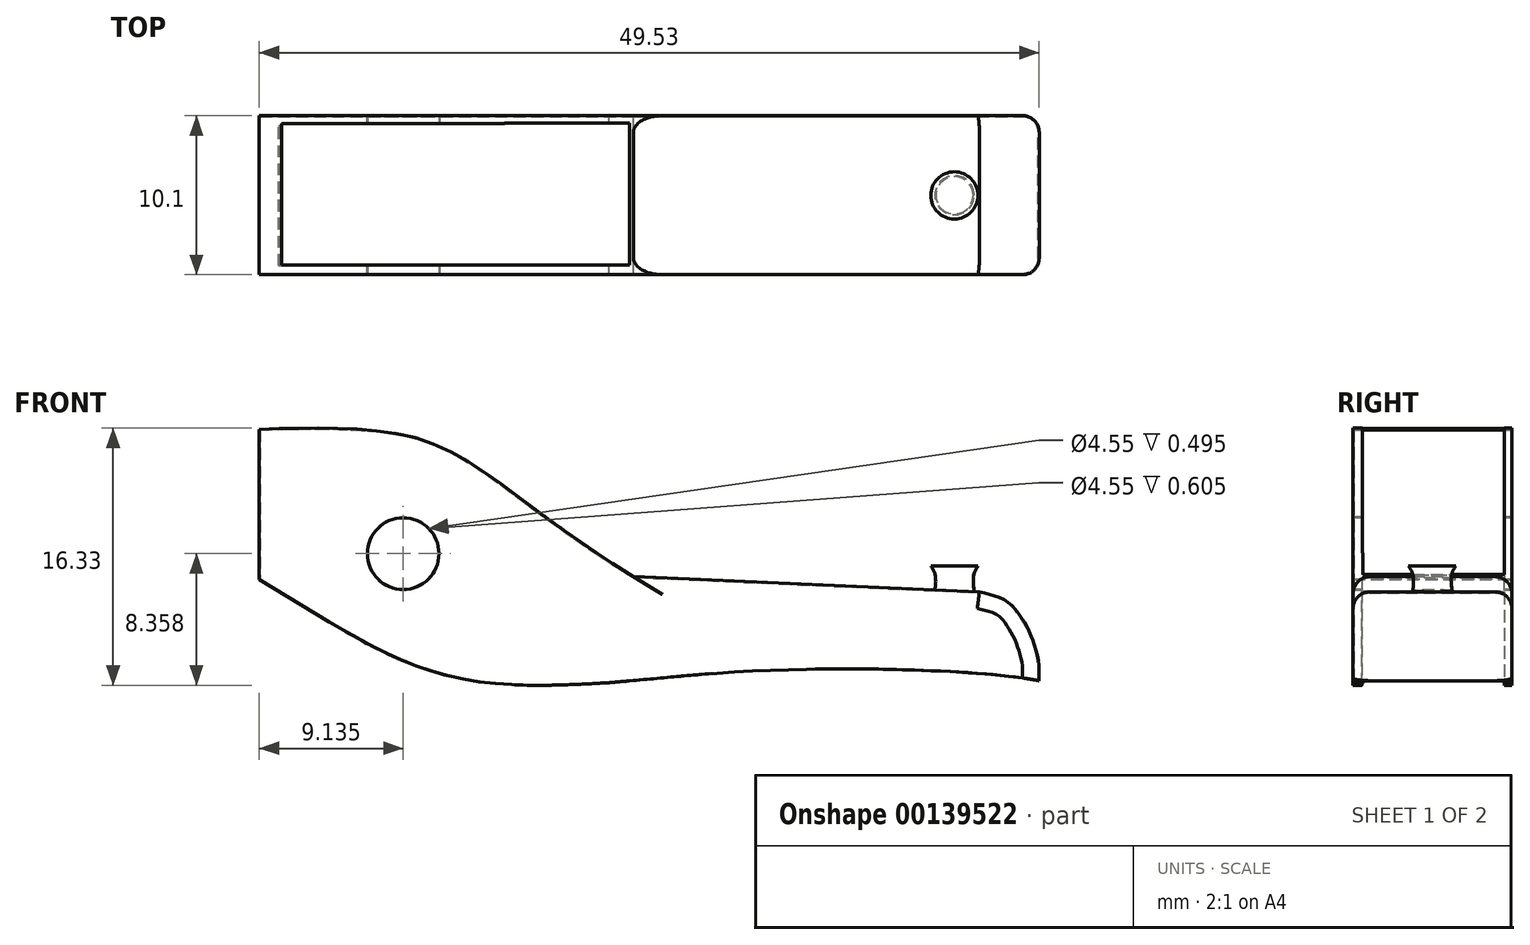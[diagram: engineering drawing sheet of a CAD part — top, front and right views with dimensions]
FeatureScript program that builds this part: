
annotation { "Feature Type Name" : "Feature", "Feature Type Description" : "" }
export const myFeature = defineFeature(function(context is Context, id is Id, definition is map)
    precondition{}
    {
        {
            var Q0;
            Q0=qCreatedBy(makeId("Front.planeOp"),FACE);
            var sketch = newSketch(context, id + "F0", { "sketchPlane" : qUnion([Q0])});
            skLineSegment(sketch, "E0", {"start": v(-18.11, 14.62) * mm, "end": v(-18.11, 5.15) * mm});
            skFitSpline(sketch, "E1", {"points": [v(-18.11, 14.62) * mm, v(-5.7, 13.04) * mm, v(5.6, 5.26) * mm], "startDerivative": vector(43.3, 1.46) * mm, "endDerivative": vector(32.79, -20.12) * mm});
            skFitSpline(sketch, "E2", {"points": [v(-18.11, 5.15) * mm, v(-6.1, -0.96) * mm, v(5.6, -1.29) * mm], "startDerivative": vector(24.76, -14.65) * mm, "endDerivative": vector(22.2, 1.12) * mm});
            skLineSegment(sketch, "E3", {"start": v(-5.7, 13.04) * mm, "end": v(-6.1, -0.96) * mm, "construction": true});
            skFitSpline(sketch, "E4", {"points": [v(5.6, -1.29) * mm, v(15.63, -0.6) * mm, v(31.3, -1.29) * mm], "startDerivative": vector(20.89, 1.84) * mm, "endDerivative": vector(17.9, -3.47) * mm});
            skLineSegment(sketch, "E5", {"start": v(5.6, 5.26) * mm, "end": v(27.57, 4.28) * mm});
            skFitSpline(sketch, "E6", {"points": [v(27.57, 4.28) * mm, v(29.94, 3.06) * mm, v(31.3, -1.29) * mm], "startDerivative": vector(9.56, -2.1) * mm, "endDerivative": vector(-1.08, -8.77) * mm});
            skLineSegment(sketch, "E7", {"start": v(-18.11, 14.62) * mm, "end": v(31.89, 14.62) * mm, "construction": true});
            skLineSegment(sketch, "E8", {"start": v(31.89, 14.62) * mm, "end": v(31.3, -1.29) * mm, "construction": true});
            skSolve(sketch);
        }
        {
            var Q0;
            Q0 = qSketchRegion(id + "F0", true);
            extrude(context, id + "F1", {"entities" : qUnion([Q0]), "depth" : 10 * mm});
        }
        {
            var Q0;
            Q0=makeQuery(id+"F1.opExtrude","CAP_FACE",FACE,{"disambiguationData":[OSD([sQuery(id+"F0.wireOp",EDGE,"E0"),sQuery(id+"F0.wireOp",EDGE,"E1"),sQuery(id+"F0.wireOp",EDGE,"E2"),sQuery(id+"F0.wireOp",EDGE,"E4"),sQuery(id+"F0.wireOp",EDGE,"E5"),sQuery(id+"F0.wireOp",EDGE,"E6")])],"isStart":false});
            var sketch = newSketch(context, id + "F2", { "sketchPlane" : qUnion([Q0])});
            skCircle(sketch, "E9", {"center": v(-9.02, 6.77) * mm, "radius": 2.32 * mm});
            skSolve(sketch);
        }
        {
            var Q0;
            Q0 = qSketchRegion(id + "F2", true);
            extrude(context, id + "F3", {"entities" : qUnion([Q0]), "operationType" : NewBodyOperationType.REMOVE, "oppositeDirection" : true, "depth" : 25 * mm});
        }
        {
            var Q0;
            Q0=makeQuery(id+"F1.opExtrude","CAP_EDGE",EDGE,{"disambiguationData":[OSD([sQuery(id+"F0.wireOp",EDGE,"E5")])],"isStart":false});
            var Q1;
            Q1=makeQuery(id+"F1.opExtrude","CAP_EDGE",EDGE,{"disambiguationData":[OSD([sQuery(id+"F0.wireOp",EDGE,"E5")])],"isStart":true});
            var Q2;
            Q2=makeQuery(id+"F1.opExtrude","CAP_EDGE",EDGE,{"disambiguationData":[OSD([sQuery(id+"F0.wireOp",EDGE,"E6")])],"isStart":false});
            var Q3;
            Q3=makeQuery(id+"F1.opExtrude","CAP_EDGE",EDGE,{"disambiguationData":[OSD([sQuery(id+"F0.wireOp",EDGE,"E6")])],"isStart":true});
            fillet(context, id + "F4", {"entities" : qUnion([Q0, Q1, Q2, Q3]), "radius" : 1 * mm, "tangentPropagation" : true, "allowEdgeOverflow" : false});
        }
        {
            var Q0;
            Q0=makeQuery(id+"F1.opExtrude","SWEPT_FACE",FACE,{"disambiguationData":[OSD([sQuery(id+"F0.wireOp",EDGE,"E4")])]});
            shell(context, id + "F5", {"entities" : qUnion([Q0]), "thickness" : 0.05 * mm, "oppositeDirection" : true});
        }
        {
            var Q0;
            Q0=qCreatedBy(makeId("Top.planeOp"),FACE);
            cPlane(context, id + "F6", {"entities" : qUnion([Q0]), "cplaneType" : CPlaneType.OFFSET, "offset" : 16 * mm, "width" : 150 * mm, "height" : 150 * mm});
        }
        {
            var Q0;
            Q0=qCreatedBy(id+"F6.planeOp",FACE);
            var sketch = newSketch(context, id + "F7", { "sketchPlane" : qUnion([Q0])});
            skLineSegment(sketch, "E10.bottom", {"start": v(-16.76, -0.44) * mm, "end": v(3.24, -0.44) * mm});
            skLineSegment(sketch, "E10.top", {"start": v(-16.76, -9.44) * mm, "end": v(3.24, -9.44) * mm});
            skLineSegment(sketch, "E10.left", {"start": v(-16.76, -0.44) * mm, "end": v(-16.76, -9.44) * mm});
            skLineSegment(sketch, "E10.right", {"start": v(3.24, -0.44) * mm, "end": v(3.24, -9.44) * mm});
            skPoint(sketch, "E10.middle", {"position": v(-6.76, -4.94) * mm});
            skSolve(sketch);
        }
        {
            var Q0;
            Q0 = qSketchRegion(id + "F7", true);
            extrude(context, id + "F8", {"entities" : qUnion([Q0]), "operationType" : NewBodyOperationType.REMOVE, "oppositeDirection" : true, "depth" : 20 * mm});
        }
        {
            var Q0;
            Q0=qCreatedBy(makeId("Top.planeOp"),FACE);
            cPlane(context, id + "F9", {"entities" : qUnion([Q0]), "cplaneType" : CPlaneType.OFFSET, "offset" : 3 * mm, "oppositeDirection" : true, "width" : 150 * mm, "height" : 150 * mm});
        }
        {
            var Q0;
            Q0=qCreatedBy(id+"F9.planeOp",FACE);
            var sketch = newSketch(context, id + "F10", { "sketchPlane" : qUnion([Q0])});
            skLineSegment(sketch, "E11.bottom", {"start": v(-17.45, -0.6) * mm, "end": v(3.47, -0.6) * mm});
            skLineSegment(sketch, "E11.top", {"start": v(-17.45, -9.48) * mm, "end": v(3.47, -9.48) * mm});
            skLineSegment(sketch, "E11.left", {"start": v(-17.45, -0.6) * mm, "end": v(-17.45, -9.48) * mm});
            skLineSegment(sketch, "E11.right", {"start": v(3.47, -0.6) * mm, "end": v(3.47, -9.48) * mm});
            skPoint(sketch, "E11.middle", {"position": v(-7, -5.04) * mm});
            skSolve(sketch);
        }
        {
            var Q0;
            Q0 = qSketchRegion(id + "F10", true);
            extrude(context, id + "F11", {"entities" : qUnion([Q0]), "operationType" : NewBodyOperationType.REMOVE, "depth" : 7.4 * mm});
        }
        {
            var Q0;
            Q0=qCreatedBy(id+"F6.planeOp",FACE);
            var sketch = newSketch(context, id + "F12", { "sketchPlane" : qUnion([Q0])});
            skLineSegment(sketch, "E12.bottom", {"start": v(-2.58, -0.44) * mm, "end": v(5.36, -0.44) * mm});
            skLineSegment(sketch, "E12.top", {"start": v(-2.58, -9.44) * mm, "end": v(5.36, -9.44) * mm});
            skLineSegment(sketch, "E12.left", {"start": v(-2.58, -0.44) * mm, "end": v(-2.58, -9.44) * mm});
            skLineSegment(sketch, "E12.right", {"start": v(5.36, -0.44) * mm, "end": v(5.36, -9.44) * mm});
            skSolve(sketch);
        }
        {
            var Q0;
            Q0 = qSketchRegion(id + "F12", true);
            extrude(context, id + "F13", {"entities" : qUnion([Q0]), "operationType" : NewBodyOperationType.REMOVE, "oppositeDirection" : true, "depth" : 50 * mm});
        }
        {
            var Q0;
            Q0=makeQuery(id+"F1.opExtrude","SWEPT_FACE",FACE,{"disambiguationData":[OSD([sQuery(id+"F0.wireOp",EDGE,"E5")])]});
            var sketch = newSketch(context, id + "F14", { "sketchPlane" : qUnion([Q0])});
            skCircle(sketch, "E13", {"center": v(25.77, -5) * mm, "radius": 1.25 * mm});
            skLineSegment(sketch, "E14", {"start": v(31.27, 0) * mm, "end": v(31.27, -10.1) * mm, "construction": true});
            skLineSegment(sketch, "E15", {"start": v(7.93, 0) * mm, "end": v(31.27, 0) * mm, "construction": true});
            skSolve(sketch);
        }
        {
            var Q0;
            Q0=qCreatedBy(makeId("Top.planeOp"),FACE);
            cPlane(context, id + "F15", {"entities" : qUnion([Q0]), "cplaneType" : CPlaneType.OFFSET, "offset" : 5.5 * mm, "width" : 150 * mm, "height" : 150 * mm});
        }
        {
            var Q0;
            Q0=qCreatedBy(id+"F15.planeOp",FACE);
            cPlane(context, id + "F16", {"entities" : qUnion([Q0]), "cplaneType" : CPlaneType.OFFSET, "offset" : 0.5 * mm, "width" : 150 * mm, "height" : 150 * mm});
        }
        {
            var Q0;
            Q0=qCreatedBy(id+"F15.planeOp",FACE);
            var sketch = newSketch(context, id + "F17", { "sketchPlane" : qUnion([Q0])});
            skCircle(sketch, "E16", {"center": v(25.99, -5.02) * mm, "radius": 1.25 * mm});
            skSolve(sketch);
        }
        {
            var Q0;
            Q0=qCreatedBy(id+"F16.planeOp",FACE);
            var sketch = newSketch(context, id + "F18", { "sketchPlane" : qUnion([Q0])});
            skCircle(sketch, "E17", {"center": v(25.99, -5.02) * mm, "radius": 1.5 * mm});
            skSolve(sketch);
        }
        {
            var Q1;
            Q1 = qSketchRegion(id + "F14", true);
            var Q2;
            Q2 = qSketchRegion(id + "F17", true);
            var Q3;
            Q3 = qSketchRegion(id + "F18", true);
            loft(context, id + "F19", {"operationType" : NewBodyOperationType.ADD, "sheetProfilesArray" : [{ "sheetProfileEntities" : qUnion([Q1]) }, { "sheetProfileEntities" : qUnion([Q2]) }, { "sheetProfileEntities" : qUnion([Q3]) }]});
        }
    });
